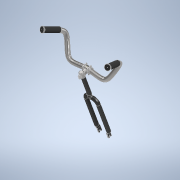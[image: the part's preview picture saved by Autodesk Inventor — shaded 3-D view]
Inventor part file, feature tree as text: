
AUTODESK INVENTOR PART (.ipt)
format: ipt  version: 2021 (Build 250183000, 183)  size: 5,266,432 bytes
history: native  units: in
note: dims shown in document units (in); Inventor stores cm internally (conversion verified against a paired STEP export)
features: plane x34, sketch x28, other x15, extrude x14, projected_geometry x9, loft x5, fillet x4, mirror x4, hole x2, split x2, sweep x1, move_body x1, chamfer x1, revolve x1
ambient origin geometry x8: Origin, YZ Plane, XZ Plane, XY Plane, X Axis, Y Axis, Z Axis, Center Point
bodies: Solid4 (feature_tree)
feature tree (121):
  sketch  "3D Sketch1"
  plane  "Work Plane6"
  sweep  "Sweep3"
  plane  "Work Plane4"
  plane  "Work Plane5"
  sketch  "Sketch14"  dims[d24=1.66in d25=0.0in d26=0.0in]
  sketch  "Sketch15"  dims[d28=2.0472in d29=0.0in d30=90.0deg d31=0.0in d32=90.0deg]
  loft  "Loft1"
  loft  "Loft2"
  plane  "Work Plane7"
  sketch  "Sketch16"  dims[d33=0.0in d34=90.0deg d35=0.0in d36=90.0deg d37=0.0in d42=180.0deg]
  plane  "Work Plane8"
  extrude  "Extrusion2"  TaperAngle=180.0deg  [1 undecoded]
  extrude  "Extrusion3"  Depth=1.378in TaperAngle=0.0deg
  plane  "Work Plane9"
  extrude  "Extrusion4"  Depth=1.7225in TaperAngle=0.0deg
  extrude  "Extrusion5"  Depth=1.1024in
  plane  "Work Plane22"
  sketch  "Sketch33"  dims[d112=0.3937in d113=0.0in d114=0.3937in d115=0.0in]
  plane  "Work Plane23"
  extrude  "Extrusion10"  Depth=0.1969in
  plane  "Work Plane19"
  plane  "Work Plane20"
  extrude  "Extrusion11"  Depth=0.4331in
  fillet  "Fillet1"  Radius=0.0197in
  plane  "Work Plane24"
  plane  "Work Plane25"
  hole  "Hole1"  [1 undecoded]
  mirror  "Mirror5"
  other  "Work Axis4"
  mirror  "Mirror3"
  plane  "Work Plane34"
  extrude  "Extrusion13"  Depth=0.3937in TaperAngle=0.0deg
  fillet  "Fillet2"  Radius=0.0984in
  plane  "Work Plane35"
  hole  "Hole2"  [1 undecoded]
  plane  "Work Plane36"
  sketch  "Sketch44"  dims[d149=1.1024in]
  split  "Split2"
  plane  "Work Plane26"
  split  "Split1"
  other  "Work Axis1"
  move_body  "Move Body2"
  plane  "Work Plane10"
  plane  "Work Plane11"
  plane  "Work Plane12"
  extrude  "Extrusion6"  [1 undecoded]
  sketch  "Sketch23"  dims[d73=0.3937in d74=0.0in d79=0.4331in d80=0.0197in]
  loft  "Loft5"
  loft  "Loft8"
  plane  "Work Plane13"
  extrude  "Extrusion8"  TaperAngle=180.0deg  [1 undecoded]
  other  "Work Axis5"
  other  "Bend Part2"
  plane  "Work Plane30"
  sketch  "Sketch36"  dims[d121=2.0in d122=0.1575in d123=0.0787in d124=90.0deg d125=1.66in d126=0.8108in]
  loft  "Loft10"
  plane  "Work Plane41"
  plane  "Work Plane31"
  extrude  "Extrusion17"  TaperAngle=90.0deg  [1 undecoded]
  plane  "Work Plane32"
  extrude  "Extrusion12"  Depth=1.38in
  chamfer  "Chamfer1"  Distance=0.7874in
  fillet  "Fillet4"  Radius=1.9685in
  mirror  "Mirror6"
  plane  "Work Plane33"
  sketch  "Sketch41"  dims[d138=1.38in d139=1.66in]
  plane  "Work Plane37"
  revolve  "Revolution2"  [1 undecoded]
  plane  "Work Plane38"
  extrude  "Extrusion14"  TaperAngle=0.0deg  [1 undecoded]
  plane  "Work Plane39"
  extrude  "Extrusion15"  Depth=0.1969in
  fillet  "Fillet3"  Radius=0.3937in
  plane  "Work Plane40"
  extrude  "Extrusion16"  Depth=0.4921in
  mirror  "Mirror7"
  sketch  "Sketch13"  dims[d19=0.0in d21=1.378in d23=1.38in]
  other  "Caña Dirección"
  sketch  "Sketch17"  dims[d43=0.3937in d44=0.0in d45=1.378in d46=0.0in]
  sketch  "Sketch18"  dims[d48=180.0deg d49=1.7225in d50=0.0in]
  sketch  "Sketch19"  dims[d53=0.8661in d54=0.0in d55=1.1024in]
  sketch  "Sketch20"  dims[d57=180.0deg d60=0.1969in]
  other  "Tubo Tenedor Central"
  sketch  "Sketch25"  dims[d85=14.9449in d86=1.38in]
  other  "Tubo Tenedor Der"
  plane  "Work Plane18"
  sketch  "Sketch32"  dims[d94=0.0in d95=90.0deg d96=0.0in d97=90.0deg d98=0.3937in d99=0.0in d105=0.0984in]
  plane  "Work Plane21"
  sketch  "Sketch34"  dims[d116=0.1969in d117=-1.0236in]
  plane  "Work Plane27"
  plane  "Work Plane28"
  sketch  "Sketch35"  dims[d119=0.1181in]
  other  "Pattern of Tubo Tenedor Der:2"
  other  "Tubo Tenedor Izq"
  plane  "Work Plane29"
  sketch  "Sketch37"  dims[d127=0.4921in d128=0.0in]
  sketch  "Sketch40"  dims[d131=90.0deg d132=180.0deg]
  sketch  "Sketch42"  dims[d140=1.66in d144=90.0deg]
  sketch  "Sketch43"  dims[d145=180.0deg d146=1.38in]
  sketch  "Sketch45"  dims[d152=1.0817in]
  other  "Copa Tenedor"
  sketch  "Sketch46"  dims[d153=90.0deg d154=0.0in d155=0.7874in d180=1.9685in]
  other  "Mango Izq"
  sketch  "Sketch47"  dims[d193=0.1969in d196=0.0in d197=0.0in]
  sketch  "Sketch48"  dims[d198=0.0in d205=0.0in]
  other  "Pattern of Mango Izq:3"
  other  "Mango Der"
  sketch  "Sketch49"  dims[d206=0.9843in d208=0.7874in d210=0.1969in d211=0.3937in d212=0.0in]
  sketch  "Sketch50"  dims[d215=0.3369in d216=0.4921in d218=0.5629in d219=0.2362in d220=0.1181in d221=0.0in d222=0.1969in d223=0.2362in d224=0.1575in d225=0.0787in d226=90.0deg d227=1.66in d228=0.8108in d229=0.0in d236=0.0in d237=90.0deg d238=0.0in d239=90.0deg d246=0.14in d247=0.315in d248=0.83in d249=90.0deg d250=-3.937in d251=1.9685in d252=5.9055in d253=0.0in d254=0.0in d255=2.1654in d256=0.3937in d257=0.0in d258=0.0787in d259=0.0in d260=0.1575in d261=0.3937in d262=0.0in d265=0.0in d266=90.0deg d269=0.3937in d270=0.0in d271=90.0deg d272=0.0in d273=0.3937in d274=0.0in d275=0.69in d276=0.7815in d277=0.1969in d278=0.0787in d279=45.0deg d280=0.0787in d141=0.0344in]
  projected_geometry  "Project Cut Edges2"
  projected_geometry  "Project Cut Edges3"
  projected_geometry  "Project Cut Edges4"
  projected_geometry  "Project Cut Edges5"
  projected_geometry  "Project Cut Edges6"
  projected_geometry  "Project Cut Edges7"
  other  "Potencia Del"
  other  "Potencia Tras"
  projected_geometry  "Project Cut Edges10"
  projected_geometry  "Project Cut Edges11"
  projected_geometry  "Project Cut Edges12"
note: 8 required parameter values undecoded (feature->parameter linkage not recoverable at this tier; creation-order binding heuristic only, values carry confidence <= 0.55)